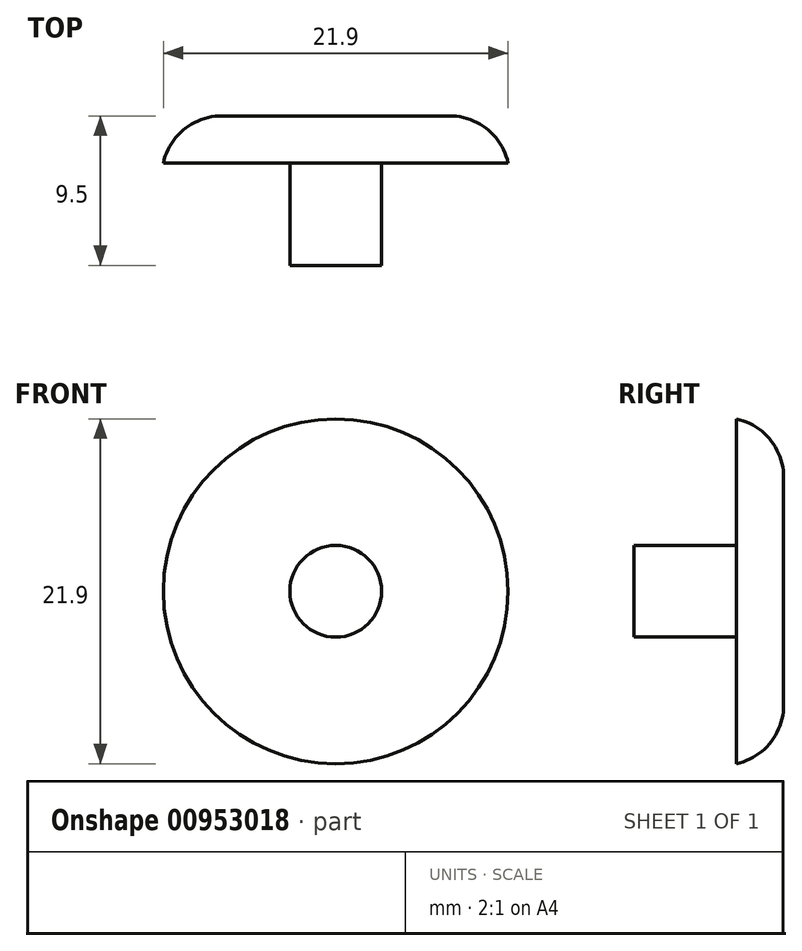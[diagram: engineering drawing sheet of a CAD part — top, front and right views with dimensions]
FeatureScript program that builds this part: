
annotation { "Feature Type Name" : "Feature", "Feature Type Description" : "" }
export const myFeature = defineFeature(function(context is Context, id is Id, definition is map)
    precondition{}
    {
        {
            var Q0;
            Q0=qCreatedBy(makeId("Front.planeOp"),FACE);
            var sketch = newSketch(context, id + "F0", { "sketchPlane" : qUnion([Q0])});
            skCircle(sketch, "E0", {"center": v(0, 0) * mm, "radius": 10.95 * mm});
            skSolve(sketch);
        }
        {
            var Q0;
            Q0=makeQuery(id+"F0.imprint","IMPRINT",FACE,{"disambiguationData":[TD([[makeQuery(id+"F0.imprint","IMPRINT",EDGE,{"derivedFrom":sQuery(id+"F0.wireOp",EDGE,"E0")}),1.0]])]});
            extrude(context, id + "F1", {"entities" : qUnion([Q0]), "depth" : 3 * mm, "offsetDistance" : 25.4 * mm});
        }
        {
            var Q0;
            Q0=makeQuery(id+"F1.opExtrude","CAP_FACE",FACE,{"disambiguationData":[OSD([sQuery(id+"F0.wireOp",EDGE,"E0")])],"isStart":false});
            var sketch = newSketch(context, id + "F2", { "sketchPlane" : qUnion([Q0])});
            skCircle(sketch, "E1", {"center": v(0, 0) * mm, "radius": 2.92 * mm});
            skSolve(sketch);
        }
        {
            var Q0;
            Q0=makeQuery(id+"F2.imprint","IMPRINT",FACE,{"disambiguationData":[TD([[makeQuery(id+"F2.imprint","IMPRINT",EDGE,{"derivedFrom":sQuery(id+"F2.wireOp",EDGE,"E1")}),1.0]])]});
            extrude(context, id + "F3", {"entities" : qUnion([Q0]), "operationType" : NewBodyOperationType.ADD, "depth" : 6.5 * mm, "offsetDistance" : 25.4 * mm});
        }
        {
            var Q0;
            Q0=makeQuery(id+"F1.opExtrude","CAP_FACE",FACE,{"disambiguationData":[OSD([sQuery(id+"F0.wireOp",EDGE,"E0")])],"isStart":true});
            fillet(context, id + "F4", {"entities" : qUnion([Q0]), "radius" : 3.8 * mm, "tangentPropagation" : true, "allowEdgeOverflow" : false});
        }
    });
